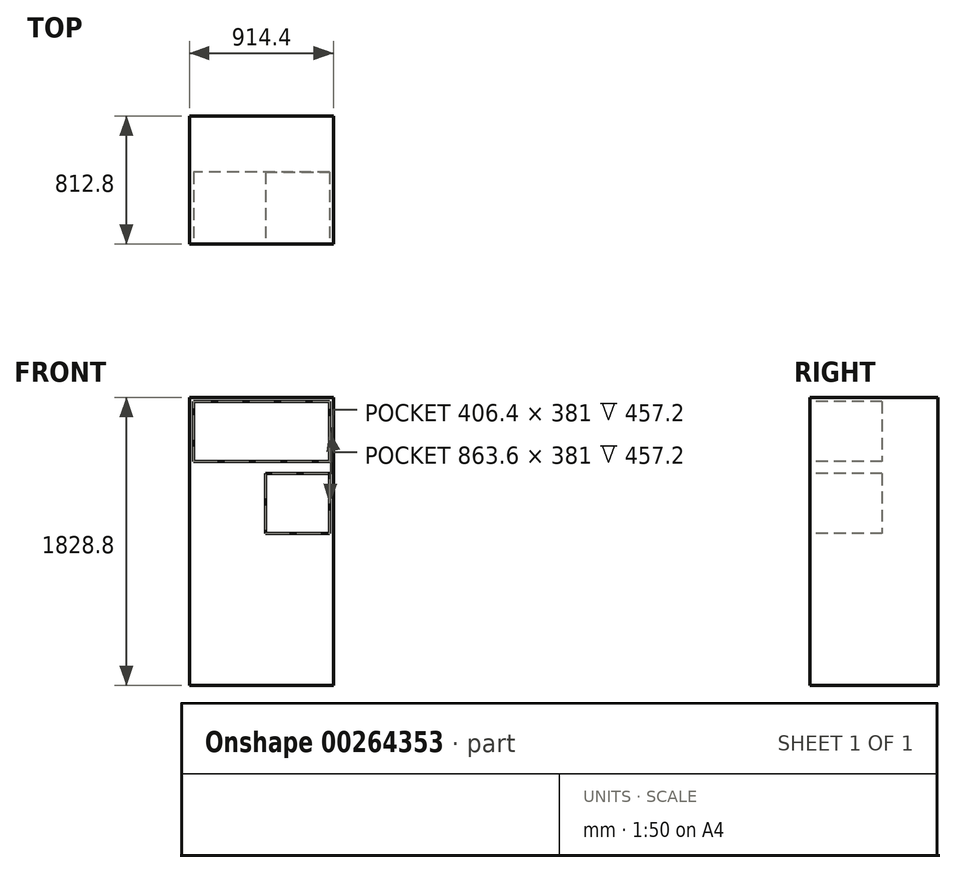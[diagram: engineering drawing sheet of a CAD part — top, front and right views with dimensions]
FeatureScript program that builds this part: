
annotation { "Feature Type Name" : "Feature", "Feature Type Description" : "" }
export const myFeature = defineFeature(function(context is Context, id is Id, definition is map)
    precondition{}
    {
        {
            var Q0;
            Q0=qCreatedBy(makeId("Front.planeOp"),FACE);
            var sketch = newSketch(context, id + "F0", { "sketchPlane" : qUnion([Q0])});
            skLineSegment(sketch, "E0.bottom", {"start": v(-457.2, 914.4) * mm, "end": v(457.2, 914.4) * mm});
            skLineSegment(sketch, "E0.top", {"start": v(-457.2, -914.4) * mm, "end": v(457.2, -914.4) * mm});
            skLineSegment(sketch, "E0.left", {"start": v(-457.2, 914.4) * mm, "end": v(-457.2, -914.4) * mm});
            skLineSegment(sketch, "E0.right", {"start": v(457.2, 914.4) * mm, "end": v(457.2, -914.4) * mm});
            skPoint(sketch, "E0.middle", {"position": v(0, 0) * mm});
            skLineSegment(sketch, "E1", {"start": v(0, 914.4) * mm, "end": v(0, -914.4) * mm});
            skSolve(sketch);
        }
        {
            var Q0;
            {var subQ0=sQuery(id+"F0.wireOp",EDGE,"E0.left");Q0=makeQuery(id+"F0.imprint","IMPRINT",FACE,{"disambiguationData":[TD([[makeQuery(id+"F0.imprint","IMPRINT",EDGE,{"derivedFrom":subQ0}),1.0]])]});}
            var Q1;
            {var subQ0=sQuery(id+"F0.wireOp",EDGE,"E0.right");Q1=makeQuery(id+"F0.imprint","IMPRINT",FACE,{"disambiguationData":[TD([[makeQuery(id+"F0.imprint","IMPRINT",EDGE,{"derivedFrom":subQ0}),-1.0]])]});}
            extrude(context, id + "F1", {"entities" : qUnion([Q0, Q1]), "oppositeDirection" : true, "depth" : 812.8 * mm});
        }
        {
            var Q0;
            Q0=makeQuery(id+"F1.opExtrude","CAP_FACE",FACE,{"disambiguationData":[OSD([sQuery(id+"F0.wireOp",EDGE,"E0.bottom"),sQuery(id+"F0.wireOp",EDGE,"E0.top"),sQuery(id+"F0.wireOp",EDGE,"E0.left"),sQuery(id+"F0.wireOp",EDGE,"E0.right")])],"isStart":true});
            var sketch = newSketch(context, id + "F2", { "sketchPlane" : qUnion([Q0])});
            skLineSegment(sketch, "E2.bottom", {"start": v(431.8, 889) * mm, "end": v(-431.8, 889) * mm});
            skLineSegment(sketch, "E2.top", {"start": v(431.8, -889) * mm, "end": v(-431.8, -889) * mm});
            skLineSegment(sketch, "E2.left", {"start": v(431.8, 889) * mm, "end": v(431.8, -889) * mm});
            skLineSegment(sketch, "E2.right", {"start": v(-431.8, 889) * mm, "end": v(-431.8, -889) * mm});
            skPoint(sketch, "E2.middle", {"position": v(0, 0) * mm});
            skLineSegment(sketch, "E3.bottom", {"start": v(-431.8, 508) * mm, "end": v(0, 508) * mm});
            skLineSegment(sketch, "E3.top", {"start": v(-431.8, 889) * mm, "end": v(0, 889) * mm});
            skLineSegment(sketch, "E3.left", {"start": v(-431.8, 508) * mm, "end": v(-431.8, 889) * mm});
            skLineSegment(sketch, "E3.right", {"start": v(0, 508) * mm, "end": v(0, 889) * mm});
            skLineSegment(sketch, "E4.bottom", {"start": v(-431.8, 508) * mm, "end": v(431.8, 508) * mm});
            skLineSegment(sketch, "E4.top", {"start": v(-431.8, 431.8) * mm, "end": v(431.8, 431.8) * mm});
            skLineSegment(sketch, "E4.left", {"start": v(-431.8, 508) * mm, "end": v(-431.8, 431.8) * mm});
            skLineSegment(sketch, "E4.right", {"start": v(431.8, 508) * mm, "end": v(431.8, 431.8) * mm});
            skLineSegment(sketch, "E5.bottom", {"start": v(0, 431.8) * mm, "end": v(-431.8, 431.8) * mm});
            skLineSegment(sketch, "E5.top", {"start": v(0, 50.8) * mm, "end": v(-431.8, 50.8) * mm});
            skLineSegment(sketch, "E5.left", {"start": v(0, 431.8) * mm, "end": v(0, 50.8) * mm});
            skLineSegment(sketch, "E5.right", {"start": v(-431.8, 431.8) * mm, "end": v(-431.8, 50.8) * mm});
            skLineSegment(sketch, "E6.MirrorCS", {"start": v(0, 50.8) * mm, "end": v(431.8, 50.8) * mm});
            skLineSegment(sketch, "E7.bottom", {"start": v(-431.8, 50.8) * mm, "end": v(431.8, 50.8) * mm});
            skLineSegment(sketch, "E7.top", {"start": v(-431.8, -25.4) * mm, "end": v(431.8, -25.4) * mm});
            skLineSegment(sketch, "E7.left", {"start": v(-431.8, 50.8) * mm, "end": v(-431.8, -25.4) * mm});
            skLineSegment(sketch, "E7.right", {"start": v(431.8, 50.8) * mm, "end": v(431.8, -25.4) * mm});
            skLineSegment(sketch, "E8.bottom", {"start": v(0, -25.4) * mm, "end": v(431.8, -25.4) * mm});
            skLineSegment(sketch, "E8.top", {"start": v(0, -406.4) * mm, "end": v(431.8, -406.4) * mm});
            skLineSegment(sketch, "E8.left", {"start": v(0, -25.4) * mm, "end": v(0, -406.4) * mm});
            skLineSegment(sketch, "E8.right", {"start": v(431.8, -25.4) * mm, "end": v(431.8, -406.4) * mm});
            skLineSegment(sketch, "E9.bottom", {"start": v(0, -25.4) * mm, "end": v(-431.8, -25.4) * mm});
            skLineSegment(sketch, "E9.top", {"start": v(0, -406.4) * mm, "end": v(-431.8, -406.4) * mm});
            skLineSegment(sketch, "E9.right", {"start": v(-431.8, -25.4) * mm, "end": v(-431.8, -406.4) * mm});
            skLineSegment(sketch, "E10.bottom", {"start": v(-431.8, -406.4) * mm, "end": v(431.8, -406.4) * mm});
            skLineSegment(sketch, "E10.top", {"start": v(-431.8, -482.6) * mm, "end": v(431.8, -482.6) * mm});
            skLineSegment(sketch, "E10.left", {"start": v(-431.8, -406.4) * mm, "end": v(-431.8, -482.6) * mm});
            skLineSegment(sketch, "E10.right", {"start": v(431.8, -406.4) * mm, "end": v(431.8, -482.6) * mm});
            skLineSegment(sketch, "E11.bottom", {"start": v(-431.8, -482.6) * mm, "end": v(0, -482.6) * mm});
            skLineSegment(sketch, "E11.top", {"start": v(-431.8, -635) * mm, "end": v(0, -635) * mm});
            skLineSegment(sketch, "E11.left", {"start": v(-431.8, -482.6) * mm, "end": v(-431.8, -635) * mm});
            skLineSegment(sketch, "E11.right", {"start": v(0, -482.6) * mm, "end": v(0, -635) * mm});
            skLineSegment(sketch, "E12.bottom", {"start": v(0, -635) * mm, "end": v(431.8, -635) * mm});
            skLineSegment(sketch, "E12.top", {"start": v(0, -482.6) * mm, "end": v(431.8, -482.6) * mm});
            skLineSegment(sketch, "E12.left", {"start": v(0, -635) * mm, "end": v(0, -482.6) * mm});
            skLineSegment(sketch, "E12.right", {"start": v(431.8, -635) * mm, "end": v(431.8, -482.6) * mm});
            skLineSegment(sketch, "E13.bottom", {"start": v(0, -635) * mm, "end": v(-431.8, -635) * mm});
            skLineSegment(sketch, "E13.top", {"start": v(0, -889) * mm, "end": v(-431.8, -889) * mm});
            skLineSegment(sketch, "E13.left", {"start": v(0, -635) * mm, "end": v(0, -889) * mm});
            skLineSegment(sketch, "E13.right", {"start": v(-431.8, -635) * mm, "end": v(-431.8, -889) * mm});
            skLineSegment(sketch, "E14.top", {"start": v(0, -889) * mm, "end": v(431.8, -889) * mm});
            skLineSegment(sketch, "E14.right", {"start": v(431.8, -635) * mm, "end": v(431.8, -889) * mm});
            skLineSegment(sketch, "E15.bottom", {"start": v(-431.8, -635) * mm, "end": v(431.8, -635) * mm});
            skLineSegment(sketch, "E15.top", {"start": v(-431.8, -736.6) * mm, "end": v(431.8, -736.6) * mm});
            skLineSegment(sketch, "E15.left", {"start": v(-431.8, -635) * mm, "end": v(-431.8, -736.6) * mm});
            skLineSegment(sketch, "E15.right", {"start": v(431.8, -635) * mm, "end": v(431.8, -736.6) * mm});
            skLineSegment(sketch, "E16.bottom", {"start": v(-25.4, 889) * mm, "end": v(25.4, 889) * mm});
            skLineSegment(sketch, "E16.top", {"start": v(-25.4, -889) * mm, "end": v(25.4, -889) * mm});
            skLineSegment(sketch, "E16.left", {"start": v(-25.4, 889) * mm, "end": v(-25.4, -889) * mm});
            skLineSegment(sketch, "E16.right", {"start": v(25.4, 889) * mm, "end": v(25.4, -889) * mm});
            skSolve(sketch);
        }
        {
            var Q0;
            {var subQ0=sQuery(id+"F2.wireOp",EDGE,"E3.top");Q0=makeQuery(id+"F2.imprint","IMPRINT",FACE,{"disambiguationData":[TD([[makeQuery(id+"F2.imprint","IMPRINT",EDGE,{"derivedFrom":subQ0}),-1.0]])]});}
            var Q1;
            {var subQ0=sQuery(id+"F2.wireOp",EDGE,"E2.bottom");Q1=makeQuery(id+"F2.imprint","IMPRINT",FACE,{"disambiguationData":[TD([[makeQuery(id+"F2.imprint","IMPRINT",EDGE,{"derivedFrom":subQ0}),1.0]])]});}
            var Q2;
            {var subQ3=sQuery(id+"F2.wireOp",EDGE,"E4.top");var subQ5=sQuery(id+"F2.wireOp",EDGE,"E16.right");var subQ6=makeQuery(id+"F2.imprint","INTERSECT",VERTEX,{"derivedFrom":[subQ3,subQ5]});Q2=makeQuery(id+"F2.imprint","IMPRINT",FACE,{"disambiguationData":[TD([[makeQuery(id+"F2.imprint","IMPRINT",EDGE,{"disambiguationData":[TD([[subQ6,-1.0]])],"derivedFrom":subQ5}),1.0]])]});}
            var Q3;
            {var subQ0=sQuery(id+"F2.wireOp",EDGE,"E5.right");Q3=makeQuery(id+"F2.imprint","IMPRINT",FACE,{"disambiguationData":[TD([[makeQuery(id+"F2.imprint","IMPRINT",EDGE,{"derivedFrom":subQ0}),1.0]])]});}
            var Q4;
            {var subQ0=sQuery(id+"F2.wireOp",EDGE,"E9.right");Q4=makeQuery(id+"F2.imprint","IMPRINT",FACE,{"disambiguationData":[TD([[makeQuery(id+"F2.imprint","IMPRINT",EDGE,{"derivedFrom":subQ0}),1.0]])]});}
            var Q5;
            {var subQ0=sQuery(id+"F2.wireOp",EDGE,"E8.right");Q5=makeQuery(id+"F2.imprint","IMPRINT",FACE,{"disambiguationData":[TD([[makeQuery(id+"F2.imprint","IMPRINT",EDGE,{"derivedFrom":subQ0}),-1.0]])]});}
            var Q6;
            {var subQ0=sQuery(id+"F2.wireOp",EDGE,"E11.left");Q6=makeQuery(id+"F2.imprint","IMPRINT",FACE,{"disambiguationData":[TD([[makeQuery(id+"F2.imprint","IMPRINT",EDGE,{"derivedFrom":subQ0}),1.0]])]});}
            var Q7;
            {var subQ0=sQuery(id+"F2.wireOp",EDGE,"E12.right");Q7=makeQuery(id+"F2.imprint","IMPRINT",FACE,{"disambiguationData":[TD([[makeQuery(id+"F2.imprint","IMPRINT",EDGE,{"derivedFrom":subQ0}),1.0]])]});}
            var Q8;
            {var subQ0=sQuery(id+"F2.wireOp",EDGE,"E13.top");Q8=makeQuery(id+"F2.imprint","IMPRINT",FACE,{"disambiguationData":[TD([[makeQuery(id+"F2.imprint","IMPRINT",EDGE,{"derivedFrom":subQ0}),-1.0]])]});}
            var Q9;
            {var subQ0=sQuery(id+"F2.wireOp",EDGE,"E14.top");Q9=makeQuery(id+"F2.imprint","IMPRINT",FACE,{"disambiguationData":[TD([[makeQuery(id+"F2.imprint","IMPRINT",EDGE,{"derivedFrom":subQ0}),1.0]])]});}
            extrude(context, id + "F3", {"entities" : qUnion([Q0, Q1, Q2, Q3, Q4, Q5, Q6, Q7, Q8, Q9]), "operationType" : NewBodyOperationType.REMOVE, "oppositeDirection" : true, "depth" : 457.2 * mm});
        }
    });
